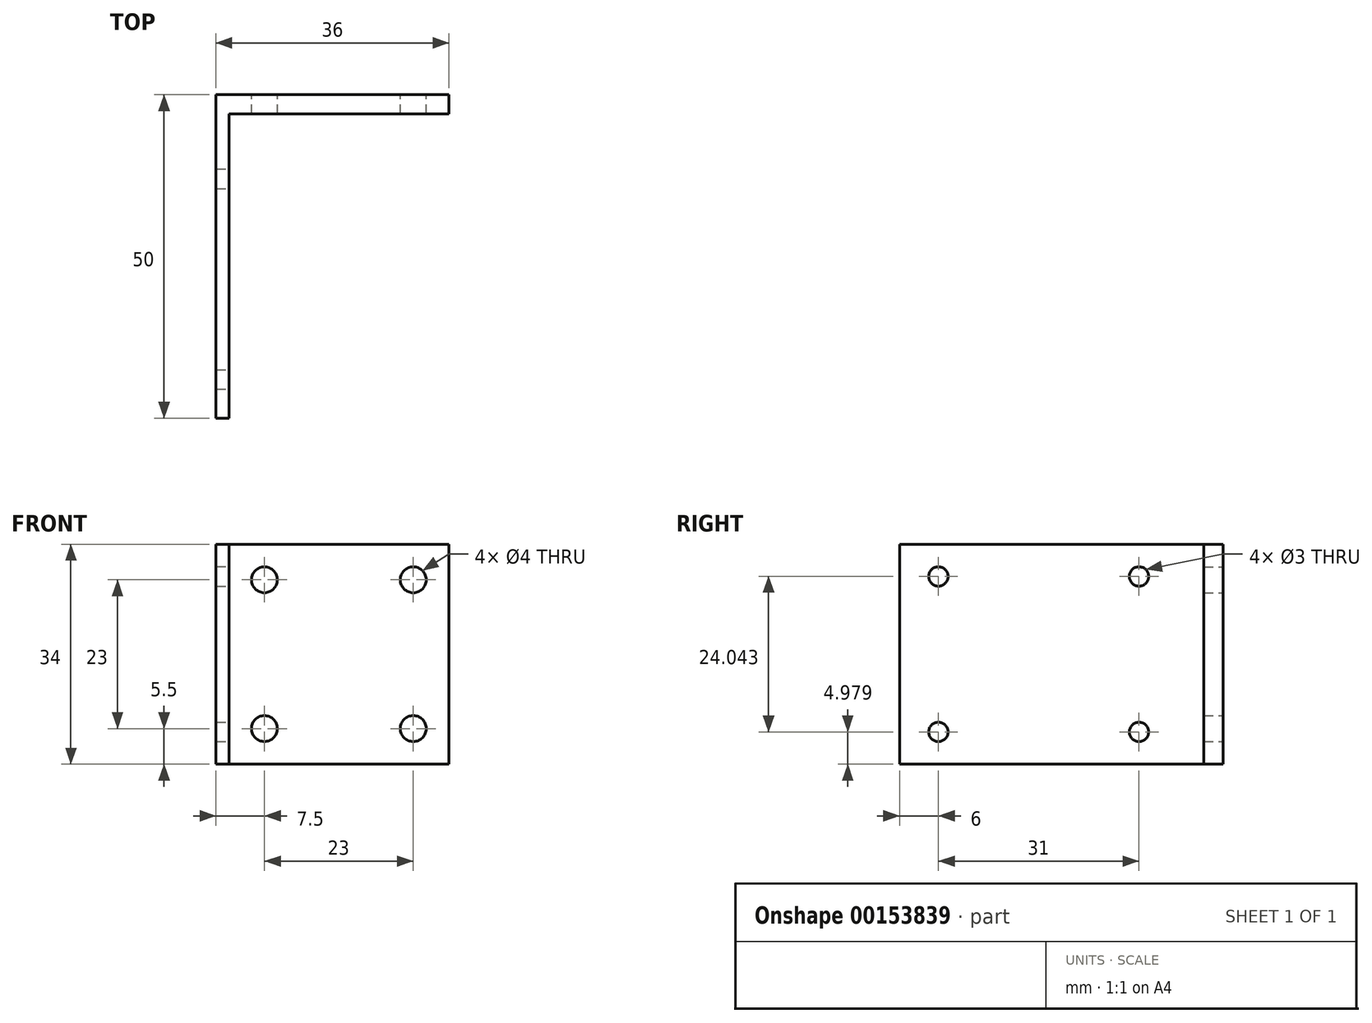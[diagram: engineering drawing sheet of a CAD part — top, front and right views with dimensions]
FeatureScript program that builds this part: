
annotation { "Feature Type Name" : "Feature", "Feature Type Description" : "" }
export const myFeature = defineFeature(function(context is Context, id is Id, definition is map)
    precondition{}
    {
        {
            var Q0;
            Q0=qCreatedBy(makeId("Front.planeOp"),FACE);
            var sketch = newSketch(context, id + "F0", { "sketchPlane" : qUnion([Q0])});
            skLineSegment(sketch, "E0.bottom", {"start": v(17, 17) * mm, "end": v(-17, 17) * mm});
            skLineSegment(sketch, "E0.top", {"start": v(17, -17) * mm, "end": v(-17, -17) * mm});
            skLineSegment(sketch, "E0.left", {"start": v(17, 17) * mm, "end": v(17, -17) * mm});
            skLineSegment(sketch, "E0.right", {"start": v(-17, 17) * mm, "end": v(-17, -17) * mm});
            skPoint(sketch, "E0.middle", {"position": v(0, 0) * mm});
            skCircle(sketch, "E1", {"center": v(-11.5, 11.5) * mm, "radius": 2 * mm});
            skLineSegment(sketch, "E2", {"start": v(0, 0) * mm, "end": v(0, 8.15) * mm, "construction": true});
            skLineSegment(sketch, "E3", {"start": v(0, 0) * mm, "end": v(7.4, 0) * mm, "construction": true});
            skCircle(sketch, "E4.MirrorC", {"center": v(11.5, 11.5) * mm, "radius": 2 * mm});
            skCircle(sketch, "E5.MirrorC", {"center": v(-11.5, -11.5) * mm, "radius": 2 * mm});
            skCircle(sketch, "E6.MirrorC", {"center": v(11.5, -11.5) * mm, "radius": 2 * mm});
            skSolve(sketch);
        }
        {
            var Q0;
            Q0=makeQuery(id+"F0.imprint","IMPRINT",FACE,{"disambiguationData":[TD([[makeQuery(id+"F0.imprint","IMPRINT",EDGE,{"derivedFrom":sQuery(id+"F0.wireOp",EDGE,"E0.bottom")}),1.0]])]});
            extrude(context, id + "F1", {"entities" : qUnion([Q0]), "depth" : 3 * mm});
        }
        {
            var Q0;
            Q0=makeQuery(id+"F1.opExtrude","SWEPT_FACE",FACE,{"disambiguationData":[OSD([sQuery(id+"F0.wireOp",EDGE,"E0.right")])]});
            var sketch = newSketch(context, id + "F2", { "sketchPlane" : qUnion([Q0])});
            skLineSegment(sketch, "E7.bottom", {"start": v(0, 17) * mm, "end": v(50, 17) * mm});
            skLineSegment(sketch, "E7.top", {"start": v(0, -17) * mm, "end": v(50, -17) * mm});
            skLineSegment(sketch, "E7.left", {"start": v(0, 17) * mm, "end": v(0, -17) * mm});
            skLineSegment(sketch, "E7.right", {"start": v(50, 17) * mm, "end": v(50, -17) * mm});
            skCircle(sketch, "E8", {"center": v(44, 12.02) * mm, "radius": 1.5 * mm});
            skLineSegment(sketch, "E9", {"start": v(28.5, 17) * mm, "end": v(28.5, -17) * mm});
            skLineSegment(sketch, "E10", {"start": v(28.5, 0) * mm, "end": v(37.62, 0) * mm});
            skPoint(sketch, "E10.endSnap0", {"position": v(28.5, 0) * mm});
            skCircle(sketch, "E11.MirrorC", {"center": v(13, 12.02) * mm, "radius": 1.5 * mm});
            skCircle(sketch, "E12.MirrorC", {"center": v(13, -12.02) * mm, "radius": 1.5 * mm});
            skCircle(sketch, "E13.MirrorC", {"center": v(44, -12.02) * mm, "radius": 1.5 * mm});
            skSolve(sketch);
        }
        {
            var Q0;
            Q0 = qSketchRegion(id + "F2", true);
            extrude(context, id + "F3", {"entities" : qUnion([Q0]), "operationType" : NewBodyOperationType.ADD, "depth" : 2 * mm});
        }
    });
